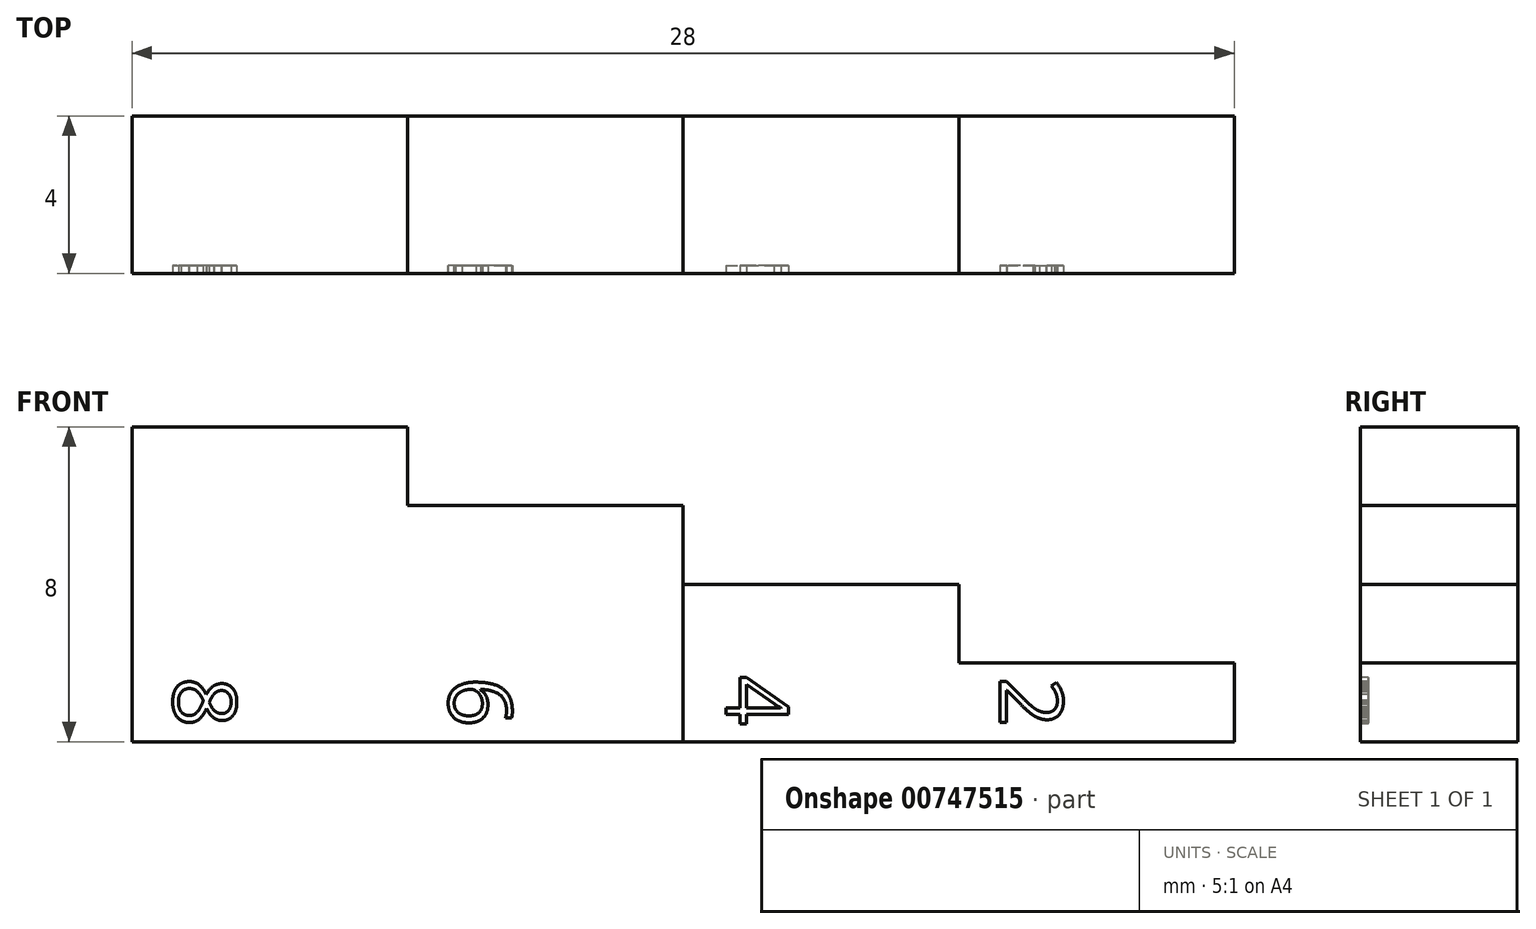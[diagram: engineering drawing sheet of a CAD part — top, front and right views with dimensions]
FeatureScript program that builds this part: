
annotation { "Feature Type Name" : "Feature", "Feature Type Description" : "" }
export const myFeature = defineFeature(function(context is Context, id is Id, definition is map)
    precondition{}
    {
        {
            var Q0;
            Q0=qCreatedBy(makeId("Top.planeOp"),FACE);
            var sketch = newSketch(context, id + "F0", { "sketchPlane" : qUnion([Q0])});
            skLineSegment(sketch, "E0.bottom", {"start": v(-40.05, -1.84) * mm, "end": v(-33.05, -1.84) * mm});
            skLineSegment(sketch, "E0.top", {"start": v(-40.05, -5.84) * mm, "end": v(-33.05, -5.84) * mm});
            skLineSegment(sketch, "E0.left", {"start": v(-40.05, -1.84) * mm, "end": v(-40.05, -5.84) * mm});
            skLineSegment(sketch, "E0.right", {"start": v(-33.05, -1.84) * mm, "end": v(-33.05, -5.84) * mm});
            skLineSegment(sketch, "E1.0", {"start": v(-26.05, -1.84) * mm, "end": v(-26.05, -5.84) * mm});
            skLineSegment(sketch, "E2.0", {"start": v(-19.05, -1.84) * mm, "end": v(-19.05, -5.84) * mm});
            skLineSegment(sketch, "E3.0", {"start": v(-12.05, -1.84) * mm, "end": v(-12.05, -5.84) * mm});
            skLineSegment(sketch, "E4", {"start": v(-33.05, -5.84) * mm, "end": v(-26.05, -5.84) * mm});
            skLineSegment(sketch, "E5", {"start": v(-19.05, -5.84) * mm, "end": v(-26.05, -5.84) * mm});
            skLineSegment(sketch, "E6", {"start": v(-19.05, -5.84) * mm, "end": v(-12.05, -5.84) * mm});
            skLineSegment(sketch, "E7", {"start": v(-12.05, -1.84) * mm, "end": v(-19.05, -1.84) * mm});
            skLineSegment(sketch, "E8", {"start": v(-19.05, -1.84) * mm, "end": v(-26.05, -1.84) * mm});
            skLineSegment(sketch, "E9", {"start": v(-26.05, -1.84) * mm, "end": v(-33.05, -1.84) * mm});
            skSolve(sketch);
        }
        {
            var Q0;
            Q0=makeQuery(id+"F0.imprint","IMPRINT",FACE,{"disambiguationData":[TD([[makeQuery(id+"F0.imprint","IMPRINT",EDGE,{"derivedFrom":sQuery(id+"F0.wireOp",EDGE,"E2.0")}),1.0]])]});
            extrude(context, id + "F1", {"entities" : qUnion([Q0]), "depth" : 2 * mm, "offsetDistance" : 25 * mm});
        }
        {
            var Q0;
            Q0=makeQuery(id+"F0.imprint","IMPRINT",FACE,{"disambiguationData":[TD([[makeQuery(id+"F0.imprint","IMPRINT",EDGE,{"derivedFrom":sQuery(id+"F0.wireOp",EDGE,"E1.0")}),1.0]])]});
            extrude(context, id + "F2", {"entities" : qUnion([Q0]), "operationType" : NewBodyOperationType.ADD, "depth" : 4 * mm, "offsetDistance" : 25 * mm});
        }
        {
            var Q0;
            Q0=makeQuery(id+"F0.imprint","IMPRINT",FACE,{"disambiguationData":[TD([[makeQuery(id+"F0.imprint","IMPRINT",EDGE,{"derivedFrom":sQuery(id+"F0.wireOp",EDGE,"E0.right")}),1.0]])]});
            extrude(context, id + "F3", {"entities" : qUnion([Q0]), "depth" : 6 * mm, "offsetDistance" : 25 * mm});
        }
        {
            var Q0;
            Q0=makeQuery(id+"F0.imprint","IMPRINT",FACE,{"disambiguationData":[TD([[makeQuery(id+"F0.imprint","IMPRINT",EDGE,{"derivedFrom":sQuery(id+"F0.wireOp",EDGE,"E0.bottom")}),-1.0]])]});
            extrude(context, id + "F4", {"entities" : qUnion([Q0]), "operationType" : NewBodyOperationType.ADD, "depth" : 8 * mm, "offsetDistance" : 25 * mm});
        }
        {
            var Q0;
            Q0=makeQuery(id+"F2.boolean.opBoolean","MERGE",FACE,{"derivedFrom":[makeQuery(id+"F1.opExtrude","SWEPT_FACE",FACE,{"disambiguationData":[OSD([sQuery(id+"F0.wireOp",EDGE,"E6")])]}),makeQuery(id+"F2.opExtrude","SWEPT_FACE",FACE,{"disambiguationData":[OSD([sQuery(id+"F0.wireOp",EDGE,"E5")])]})]});
            var sketch = newSketch(context, id + "F5", { "sketchPlane" : qUnion([Q0])});
            skLineSegment(sketch, "E10.0", {"start": v(-12.45, 0.2) * mm, "end": v(-18.65, 0.2) * mm});
            skLineSegment(sketch, "E11.0", {"start": v(-12.45, 1.8) * mm, "end": v(-18.65, 1.8) * mm});
            skLineSegment(sketch, "E12.0", {"start": v(-12.45, 0.2) * mm, "end": v(-12.45, 1.8) * mm});
            skLineSegment(sketch, "E13.0", {"start": v(-18.65, 0.2) * mm, "end": v(-18.65, 1.8) * mm});
            skLineSegment(sketch, "E14.0", {"start": v(-19.45, 0.2) * mm, "end": v(-19.45, 1.8) * mm});
            skLineSegment(sketch, "E15.0", {"start": v(-25.65, 0.2) * mm, "end": v(-25.65, 1.8) * mm});
            skLineSegment(sketch, "E16.0", {"start": v(-26.45, 0.2) * mm, "end": v(-26.45, 1.8) * mm});
            skLineSegment(sketch, "E17.0", {"start": v(-32.65, 0.2) * mm, "end": v(-32.65, 1.8) * mm});
            skLineSegment(sketch, "E18.0", {"start": v(-33.45, 0.2) * mm, "end": v(-33.45, 1.8) * mm});
            skLineSegment(sketch, "E19.0", {"start": v(-39.65, 0.2) * mm, "end": v(-39.65, 1.8) * mm});
            skLineSegment(sketch, "E20.trimOffspring", {"start": v(-33.45, 1.8) * mm, "end": v(-39.65, 1.8) * mm});
            skLineSegment(sketch, "E21.trimOffspring", {"start": v(-33.45, 0.2) * mm, "end": v(-39.65, 0.2) * mm});
            skLineSegment(sketch, "E22.trimOffspring", {"start": v(-26.45, 1.8) * mm, "end": v(-32.65, 1.8) * mm});
            skLineSegment(sketch, "E23.trimOffspring", {"start": v(-26.45, 0.2) * mm, "end": v(-32.65, 0.2) * mm});
            skLineSegment(sketch, "E24.trimOffspring", {"start": v(-19.45, 1.8) * mm, "end": v(-25.65, 1.8) * mm});
            skLineSegment(sketch, "E25.trimOffspring", {"start": v(-19.45, 0.2) * mm, "end": v(-25.65, 0.2) * mm});
            skLineSegment(sketch, "E26", {"start": v(-26.05, 1.8) * mm, "end": v(-26.05, 0) * mm});
            skText(sketch, "E27", { "text": "2", "fontName": "OpenSans-Regular.ttf"});
            skText(sketch, "E28", { "text": "4", "fontName": "OpenSans-Regular.ttf"});
            skText(sketch, "E29", { "text": "6", "fontName": "OpenSans-Regular.ttf"});
            skText(sketch, "E30", { "text": "8", "fontName": "OpenSans-Regular.ttf"});
            const initialGuessF5  = {"E27": [-0.018, 0.00164, 0, -1, 0.0016], "E28": [-0.02497, 0.00168, 0, -1, 0.0016], "E29": [-0.032, 0.00164, 0, -1, 0.0016], "E30": [-0.039, 0.00164, 0, -1, 0.0016]};
            skSetInitialGuess(sketch, initialGuessF5);
            skSolve(sketch);
        }
        {
            var Q0;
            Q0=makeQuery(id+"F5.imprint","IMPRINT",FACE,{"disambiguationData":[TD([[makeQuery(id+"F5.imprint","IMPRINT",EDGE,{"derivedFrom":sQuery(id+"F5.wireOp",EDGE,"E27.sketch_text.stroke-0")}),-1.0]])]});
            var Q1;
            Q1=makeQuery(id+"F5.imprint","IMPRINT",FACE,{"disambiguationData":[TD([[makeQuery(id+"F5.imprint","IMPRINT",EDGE,{"derivedFrom":sQuery(id+"F5.wireOp",EDGE,"E28.sketch_text.stroke-0")}),-1.0]])]});
            extrude(context, id + "F6", {"entities" : qUnion([Q0, Q1]), "operationType" : NewBodyOperationType.REMOVE, "oppositeDirection" : true, "depth" : .2 * mm, "offsetDistance" : 25 * mm});
        }
        {
            var Q0;
            Q0=makeQuery(id+"F5.imprint","IMPRINT",FACE,{"disambiguationData":[TD([[makeQuery(id+"F5.imprint","IMPRINT",EDGE,{"derivedFrom":sQuery(id+"F5.wireOp",EDGE,"E30.sketch_text.stroke-0")}),-1.0]])]});
            var Q1;
            Q1=makeQuery(id+"F5.imprint","IMPRINT",FACE,{"disambiguationData":[TD([[makeQuery(id+"F5.imprint","IMPRINT",EDGE,{"derivedFrom":sQuery(id+"F5.wireOp",EDGE,"E29.sketch_text.stroke-0")}),-1.0]])]});
            extrude(context, id + "F7", {"entities" : qUnion([Q0, Q1]), "operationType" : NewBodyOperationType.REMOVE, "oppositeDirection" : true, "depth" : .2 * mm, "offsetDistance" : 25 * mm});
        }
    });
